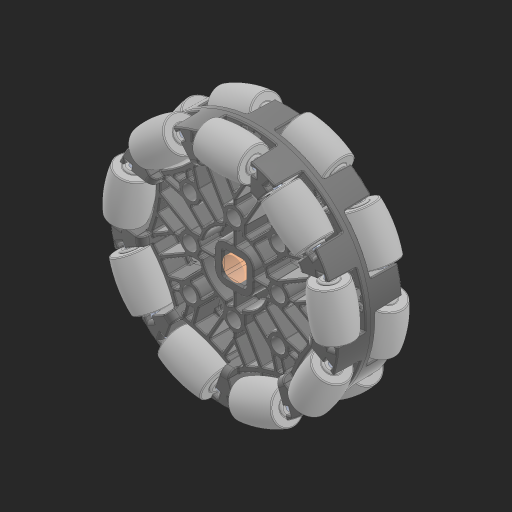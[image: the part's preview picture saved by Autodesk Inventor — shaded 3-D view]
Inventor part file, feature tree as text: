
AUTODESK INVENTOR PART (.ipt)
format: ipt  version: 2023 (Build 270158000, 158)  size: 32,808,960 bytes
history: native  units: in
note: dims shown in document units (in); Inventor stores cm internally (conversion verified against a paired STEP export)
features: other x57, move_body x1, sketch x1, extrude x1
ambient origin geometry x8: Origin, YZ Plane, XZ Plane, XY Plane, X Axis, Y Axis, Z Axis, Center Point
bodies: Solid1 (feature_tree), Solid2 (feature_tree), Solid3 (feature_tree), Solid4 (feature_tree), Solid5 (feature_tree), Solid6 (feature_tree), Solid7 (feature_tree), Solid8 (feature_tree), Solid9 (feature_tree), Solid10 (feature_tree), Solid11 (feature_tree), Solid12 (feature_tree), Solid13 (feature_tree), Solid14 (feature_tree), Solid15 (feature_tree), Solid16 (feature_tree), Solid17 (feature_tree), Solid18 (feature_tree), Solid19 (feature_tree), Solid20 (feature_tree), Solid21 (feature_tree), Solid22 (feature_tree), Solid23 (feature_tree), Solid24 (feature_tree), Solid25 (feature_tree), Solid26 (feature_tree), Solid27 (feature_tree), Solid28 (feature_tree), Solid29 (feature_tree), Solid30 (feature_tree), Solid31 (feature_tree), Solid32 (feature_tree), Solid33 (feature_tree), Solid34 (feature_tree), Solid35 (feature_tree), Solid36 (feature_tree), Solid37 (feature_tree), Solid38 (feature_tree), Solid39 (feature_tree), Solid40 (feature_tree), Solid41 (feature_tree), Solid42 (feature_tree), Solid43 (feature_tree), Solid44 (feature_tree), Solid45 (feature_tree), Solid46 (feature_tree), Solid47 (feature_tree), Solid48 (feature_tree), Solid49 (feature_tree), Solid50 (feature_tree), Solid51 (feature_tree), Solid52 (feature_tree), Solid53 (feature_tree), Solid54 (feature_tree), Solid55 (feature_tree)
feature tree (60):
  other  "2.75 (220mm Travel) Omni-Directional Anti-Static Wheel (276-8106).iam"
  other  "276-8106-001 Rev1.ipt:1"
  other  "276-8106-002 Rev1.iam:1::276-3526-001 Rev1.ipt:1"
  other  "276-8106-002 Rev1.iam:1::276-3526-003 Rev1.ipt:1"
  other  "276-8106-002 Rev1.iam:1::276-8106-003 Rev1.ipt:1"
  other  "276-8106-002 Rev1_1.iam:1::276-3526-001 Rev1.ipt:1"
  other  "276-8106-002 Rev1_1.iam:1::276-3526-003 Rev1.ipt:1"
  other  "276-8106-002 Rev1_1.iam:1::276-8106-003 Rev1.ipt:1"
  other  "276-8106-002 Rev1_2.iam:1::276-3526-001 Rev1.ipt:1"
  other  "276-8106-002 Rev1_2.iam:1::276-3526-003 Rev1.ipt:1"
  other  "276-8106-002 Rev1_2.iam:1::276-8106-003 Rev1.ipt:1"
  other  "276-8106-002 Rev1_3.iam:1::276-3526-001 Rev1.ipt:1"
  other  "276-8106-002 Rev1_3.iam:1::276-3526-003 Rev1.ipt:1"
  other  "276-8106-002 Rev1_3.iam:1::276-8106-003 Rev1.ipt:1"
  other  "276-8106-002 Rev1_4.iam:1::276-3526-001 Rev1.ipt:1"
  other  "276-8106-002 Rev1_4.iam:1::276-3526-003 Rev1.ipt:1"
  other  "276-8106-002 Rev1_4.iam:1::276-8106-003 Rev1.ipt:1"
  other  "276-8106-002 Rev1_5.iam:1::276-3526-001 Rev1.ipt:1"
  other  "276-8106-002 Rev1_5.iam:1::276-3526-003 Rev1.ipt:1"
  other  "276-8106-002 Rev1_5.iam:1::276-8106-003 Rev1.ipt:1"
  other  "276-8106-002 Rev1_6.iam:1::276-3526-001 Rev1.ipt:1"
  other  "276-8106-002 Rev1_6.iam:1::276-3526-003 Rev1.ipt:1"
  other  "276-8106-002 Rev1_6.iam:1::276-8106-003 Rev1.ipt:1"
  other  "276-8106-002 Rev1_7.iam:1::276-3526-001 Rev1.ipt:1"
  other  "276-8106-002 Rev1_7.iam:1::276-3526-003 Rev1.ipt:1"
  other  "276-8106-002 Rev1_7.iam:1::276-8106-003 Rev1.ipt:1"
  other  "276-8106-002 Rev1_8.iam:1::276-3526-001 Rev1.ipt:1"
  other  "276-8106-002 Rev1_8.iam:1::276-3526-003 Rev1.ipt:1"
  other  "276-8106-002 Rev1_8.iam:1::276-8106-003 Rev1.ipt:1"
  other  "276-8106-002 Rev1_9.iam:1::276-3526-001 Rev1.ipt:1"
  other  "276-8106-002 Rev1_9.iam:1::276-3526-003 Rev1.ipt:1"
  other  "276-8106-002 Rev1_9.iam:1::276-8106-003 Rev1.ipt:1"
  other  "276-8106-002 Rev1_10.iam:1::276-3526-001 Rev1.ipt:1"
  other  "276-8106-002 Rev1_10.iam:1::276-3526-003 Rev1.ipt:1"
  other  "276-8106-002 Rev1_10.iam:1::276-8106-003 Rev1.ipt:1"
  other  "276-8106-002 Rev1_11.iam:1::276-3526-001 Rev1.ipt:1"
  other  "276-8106-002 Rev1_11.iam:1::276-3526-003 Rev1.ipt:1"
  other  "276-8106-002 Rev1_11.iam:1::276-8106-003 Rev1.ipt:1"
  other  "276-8106-002 Rev1_12.iam:1::276-3526-001 Rev1.ipt:1"
  other  "276-8106-002 Rev1_12.iam:1::276-3526-003 Rev1.ipt:1"
  other  "276-8106-002 Rev1_12.iam:1::276-8106-003 Rev1.ipt:1"
  other  "276-8106-002 Rev1_13.iam:1::276-3526-001 Rev1.ipt:1"
  other  "276-8106-002 Rev1_13.iam:1::276-3526-003 Rev1.ipt:1"
  other  "276-8106-002 Rev1_13.iam:1::276-8106-003 Rev1.ipt:1"
  other  "276-8106-002 Rev1_14.iam:1::276-3526-001 Rev1.ipt:1"
  other  "276-8106-002 Rev1_14.iam:1::276-3526-003 Rev1.ipt:1"
  other  "276-8106-002 Rev1_14.iam:1::276-8106-003 Rev1.ipt:1"
  other  "276-8106-002 Rev1_15.iam:1::276-3526-001 Rev1.ipt:1"
  other  "276-8106-002 Rev1_15.iam:1::276-3526-003 Rev1.ipt:1"
  other  "276-8106-002 Rev1_15.iam:1::276-8106-003 Rev1.ipt:1"
  other  "276-8106-002 Rev1_16.iam:1::276-3526-001 Rev1.ipt:1"
  other  "276-8106-002 Rev1_16.iam:1::276-3526-003 Rev1.ipt:1"
  other  "276-8106-002 Rev1_16.iam:1::276-8106-003 Rev1.ipt:1"
  other  "276-8106-002 Rev1_17.iam:1::276-3526-001 Rev1.ipt:1"
  other  "276-8106-002 Rev1_17.iam:1::276-3526-003 Rev1.ipt:1"
  other  "276-8106-002 Rev1_17.iam:1::276-8106-003 Rev1.ipt:1"
  move_body  "Move Body1"
  sketch  "Sketch1"  dims[d0=0.3937in d1=90.0deg d2=0.25in d3=1.0in d4=0.0in]
  other  "Srf1"
  extrude  "ExtrusionSrf1"  TaperAngle=90.0deg  [1 undecoded]
note: 1 required parameter value undecoded (feature->parameter linkage not recoverable at this tier; creation-order binding heuristic only, values carry confidence <= 0.55)
